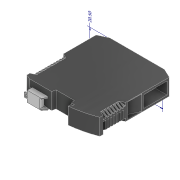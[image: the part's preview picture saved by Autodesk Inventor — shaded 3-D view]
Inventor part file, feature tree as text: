
AUTODESK INVENTOR PART (.ipt)
format: ipt  version: 2022 (Build 260153000, 153)  size: 687,616 bytes
history: native  units: mm
features: sketch x33, extrude x27, projected_geometry x7, plane x6, other x5, loft x2, mirror x2
ambient origin geometry x8: Origin, YZ Plane, XZ Plane, XY Plane, X Axis, Y Axis, Z Axis, Center Point
bodies: Solid1 (feature_tree), Solid2 (feature_tree), Solid3 (feature_tree)
feature tree (82):
  other  "Annotations"
  extrude  "Extrusion1"  Depth=110.0mm
  extrude  "Extrusion2"  Depth=14.0mm
  loft  "Loft1"
  plane  "Work Plane1"
  plane  "Work Plane2"
  mirror  "Mirror1"
  extrude  "Extrusion3"  Depth=7.0mm
  extrude  "Extrusion4"  Depth=7.0mm
  extrude  "Extrusion5"  Depth=7.0mm
  extrude  "Extrusion6"  Depth=22.5mm TaperAngle=0.0deg
  extrude  "Extrusion7"  Depth=7.0mm
  extrude  "Extrusion8"  Depth=7.0mm
  sketch  "Sketch14"  dims[d22=0.0mm d23=90.0deg d24=0.0mm d25=90.0deg]
  extrude  "Extrusion9"  Depth=4.0mm
  extrude  "Extrusion10"  TaperAngle=0.0deg  [1 undecoded]
  loft  "Loft2"
  mirror  "Mirror2"
  extrude  "Extrusion11"  [1 undecoded]
  extrude  "Extrusion12"  Depth=3.0mm
  extrude  "Extrusion13"  Depth=16.65mm
  extrude  "Extrusion14"  TaperAngle=0.0deg  [1 undecoded]
  extrude  "Extrusion15"  Depth=0.85mm TaperAngle=0.0deg
  extrude  "Extrusion16"  Depth=1.0mm
  extrude  "Extrusion17"  Depth=1.0mm
  extrude  "Extrusion18"  Depth=1.5mm TaperAngle=0.0deg
  extrude  "Extrusion19"  Depth=2.0mm
  extrude  "Extrusion20"  Depth=2.0mm
  extrude  "Extrusion21"  Depth=2.0mm
  extrude  "Extrusion22"  Depth=2.0mm
  extrude  "Extrusion23"  Depth=2.0mm
  plane  "Work Plane4"
  extrude  "Extrusion24"  Depth=2.0mm
  extrude  "Extrusion25"  TaperAngle=0.0deg  [1 undecoded]
  plane  "Work Plane5"
  extrude  "Extrusion26"  Depth=7.0mm
  plane  "Work Plane6"
  extrude  "Extrusion27"  TaperAngle=90.0deg  [1 undecoded]
  other  "Decal1"
  sketch  "Sketch1"  dims[d0=100.0mm d1=110.0mm]
  sketch  "Sketch2"  dims[d2=22.5mm d3=0.0mm d4=14.0mm]
  sketch  "Sketch3"  dims[d5=14.0mm d6=0.0mm]
  sketch  "Sketch4"  dims[d7=7.0mm d8=4.363323mm]
  sketch  "Sketch8"  dims[d9=25.0mm d10=7.0mm]
  sketch  "Sketch9"  dims[d11=7.0mm d12=27.052603mm]
  sketch  "Sketch10"  dims[d13=25.0mm d14=22.5mm d15=0.0mm]
  sketch  "Sketch11"  dims[d16=7.0mm d17=27.052603mm]
  projected_geometry  "Projected Loop2"
  sketch  "Sketch12"  dims[d18=25.0mm d19=7.0mm]
  sketch  "Sketch13"  dims[d20=7.0mm d21=4.0mm]
  projected_geometry  "Projected Loop3"
  sketch  "Sketch15"  dims[d26=35.434889mm d27=4.518234mm]
  sketch  "Sketch16"  dims[d36=-50.0mm d37=-11.25mm]
  sketch  "Sketch17"  dims[d38=3.0mm d39=8.325mm]
  sketch  "Sketch18"  dims[d40=31.8mm d41=16.65mm]
  plane  "Work Plane3"
  sketch  "Sketch19"  dims[d42=16.2mm d43=0.0mm d44=0.0mm d45=0.0mm]
  sketch  "Sketch20"  dims[d46=0.85mm d47=0.0mm d48=0.85mm d49=0.0mm]
  sketch  "Sketch21"  dims[d50=2.0mm d51=1.0mm]
  sketch  "Sketch22"  dims[d52=2.0mm d53=1.0mm]
  sketch  "Sketch23"  dims[d54=1.5mm d55=0.0mm d56=1.5mm d57=0.0mm]
  sketch  "Sketch24"  dims[d58=1.0mm d59=2.0mm]
  sketch  "Sketch25"  dims[d60=2.0mm d61=2.0mm]
  projected_geometry  "Projected Loop4"
  sketch  "Sketch26"  dims[d62=2.0mm d63=2.0mm]
  projected_geometry  "Projected Loop5"
  sketch  "Sketch27"  dims[d64=2.0mm d65=2.0mm]
  sketch  "Sketch28"  dims[d66=2.0mm d67=2.0mm]
  sketch  "Sketch29"  dims[d68=2.0mm d69=2.0mm]
  sketch  "Sketch30"  dims[d70=2.0mm d71=0.0mm d72=0.0mm]
  projected_geometry  "Projected Loop6"
  sketch  "Sketch31"  dims[d73=2.0mm d74=0.0mm d75=7.0mm]
  projected_geometry  "Projected Loop7"
  sketch  "Sketch32"  dims[d76=40.0mm d77=90.0deg]
  sketch  "Sketch33"  dims[d78=7.0mm]
  sketch  "Sketch34"  dims[d79=4.0mm]
  sketch  "Sketch35"  dims[d80=0.0mm d81=90.0deg]
  projected_geometry  "Projected Loop8"
  sketch  "Sketch36"  dims[d82=0.0mm d83=90.0deg d84=2.0mm d85=2.0mm d86=2.0mm d87=2.0mm d88=2.0mm d89=2.0mm d90=2.0mm d91=2.0mm d92=0.0mm d93=0.0mm d94=2.0mm d95=0.0mm d96=11.25mm d97=22.0mm d98=44.0mm d99=14.5mm d100=9.0mm d101=0.0mm d102=11.5mm d103=3.0mm d104=25.307274mm d105=5.0mm d106=0.0mm d107=0.0mm d108=1.0mm d109=1.0mm d110=0.0mm d111=0.0mm d112=10.0mm d113=0.0mm d114=0.0mm d115=0.0mm d116=8.0mm d117=0.0mm d118=0.0mm d119=0.0mm d120=1.0mm d121=6.0mm d122=10.0mm d123=0.0mm d124=1.0mm d125=1.0mm d126=1.0mm d127=1.0mm d128=10.5mm d129=16.25mm d130=0.0mm d131=16.25mm d132=0.0mm d133=7.25mm d134=3.0mm d135=4.0mm d136=6.0mm d137=1.0mm d138=2.0mm d139=4.0mm d140=16.25mm d141=0.0mm d142=1.1mm d143=0.6mm d144=0.6mm d145=4.7mm d146=0.0mm d147=4.7mm d148=0.0mm d149=-12.5mm d150=6.0mm d151=1.0mm d152=0.0mm d153=-2.0mm d154=1.0mm d155=0.0mm d156=1.377079mm d157=7.860714mm d158=70.643649mm d159=0.0mm d160=10.0mm d161=20.5mm]
  other  "Image1"
  other  "Linear Dimension 1"
  other  "Linear Dimension 2"
note: 5 required parameter values undecoded (feature->parameter linkage not recoverable at this tier; creation-order binding heuristic only, values carry confidence <= 0.55)
